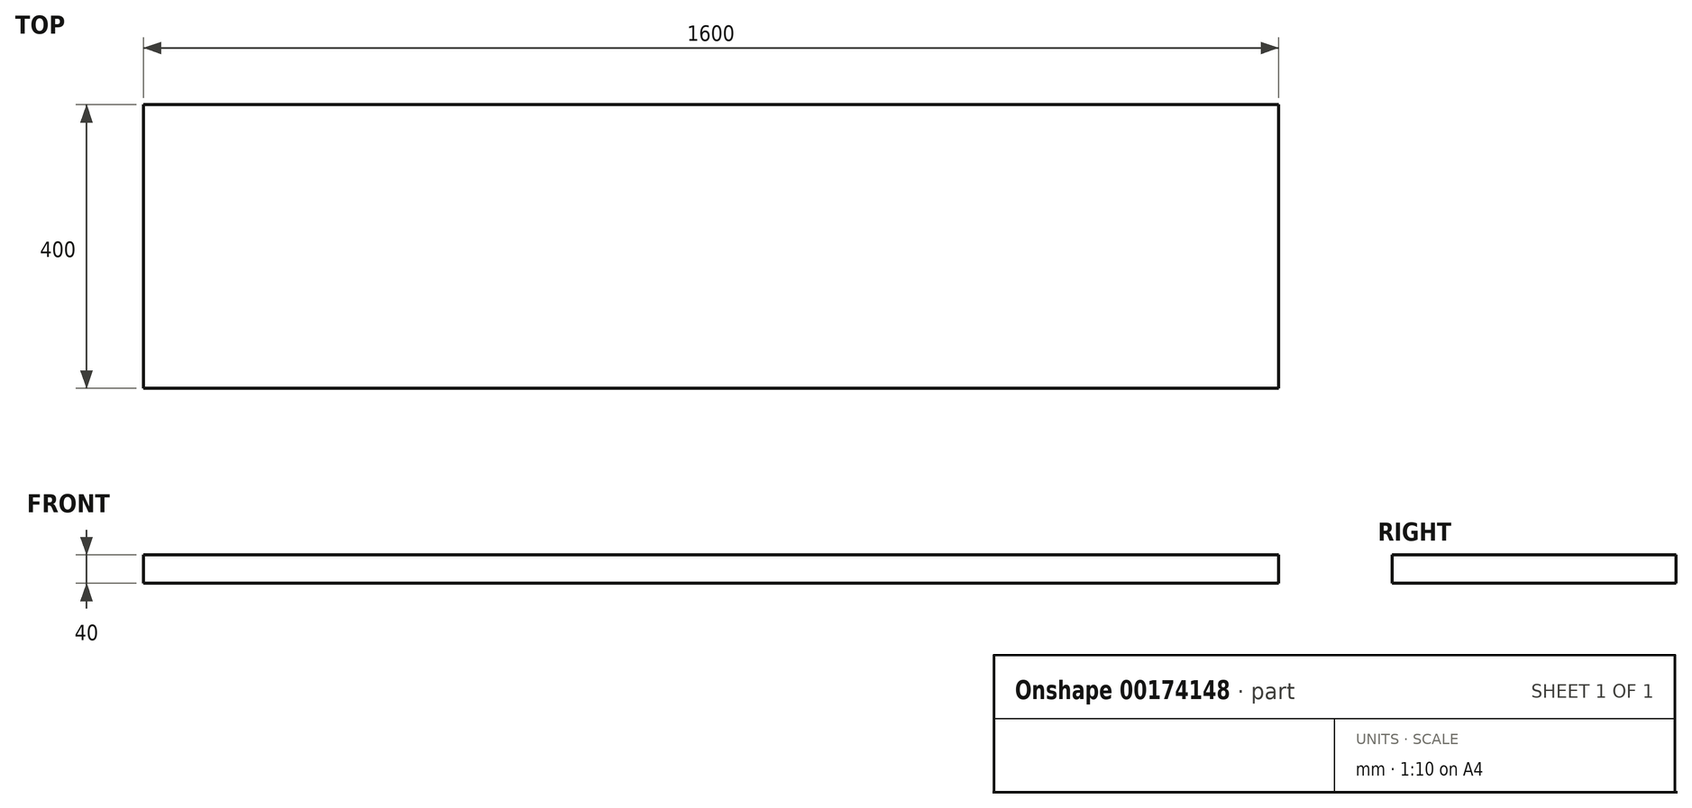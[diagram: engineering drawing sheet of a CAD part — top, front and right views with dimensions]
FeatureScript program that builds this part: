
annotation { "Feature Type Name" : "Feature", "Feature Type Description" : "" }
export const myFeature = defineFeature(function(context is Context, id is Id, definition is map)
    precondition{}
    {
        {
            var Q0;
            Q0=qCreatedBy(makeId("Top.planeOp"),FACE);
            var sketch = newSketch(context, id + "F0", { "sketchPlane" : qUnion([Q0])});
            skLineSegment(sketch, "E0.bottom", {"start": v(0, 0) * mm, "end": v(1600, 0) * mm});
            skLineSegment(sketch, "E0.top", {"start": v(0, 400) * mm, "end": v(1600, 400) * mm});
            skLineSegment(sketch, "E0.left", {"start": v(0, 0) * mm, "end": v(0, 400) * mm});
            skLineSegment(sketch, "E0.right", {"start": v(1600, 0) * mm, "end": v(1600, 400) * mm});
            skPoint(sketch, "E1.orphan", {"position": v(1600, 400) * mm});
            skSolve(sketch);
        }
        {
            var Q0;
            Q0=makeQuery(id+"F0.imprint","IMPRINT",FACE,{"disambiguationData":[TD([[makeQuery(id+"F0.imprint","IMPRINT",EDGE,{"derivedFrom":sQuery(id+"F0.wireOp",EDGE,"E0.bottom")}),1.0]])]});
            extrude(context, id + "F1", {"entities" : qUnion([Q0]), "depth" : 40 * mm});
        }
    });
